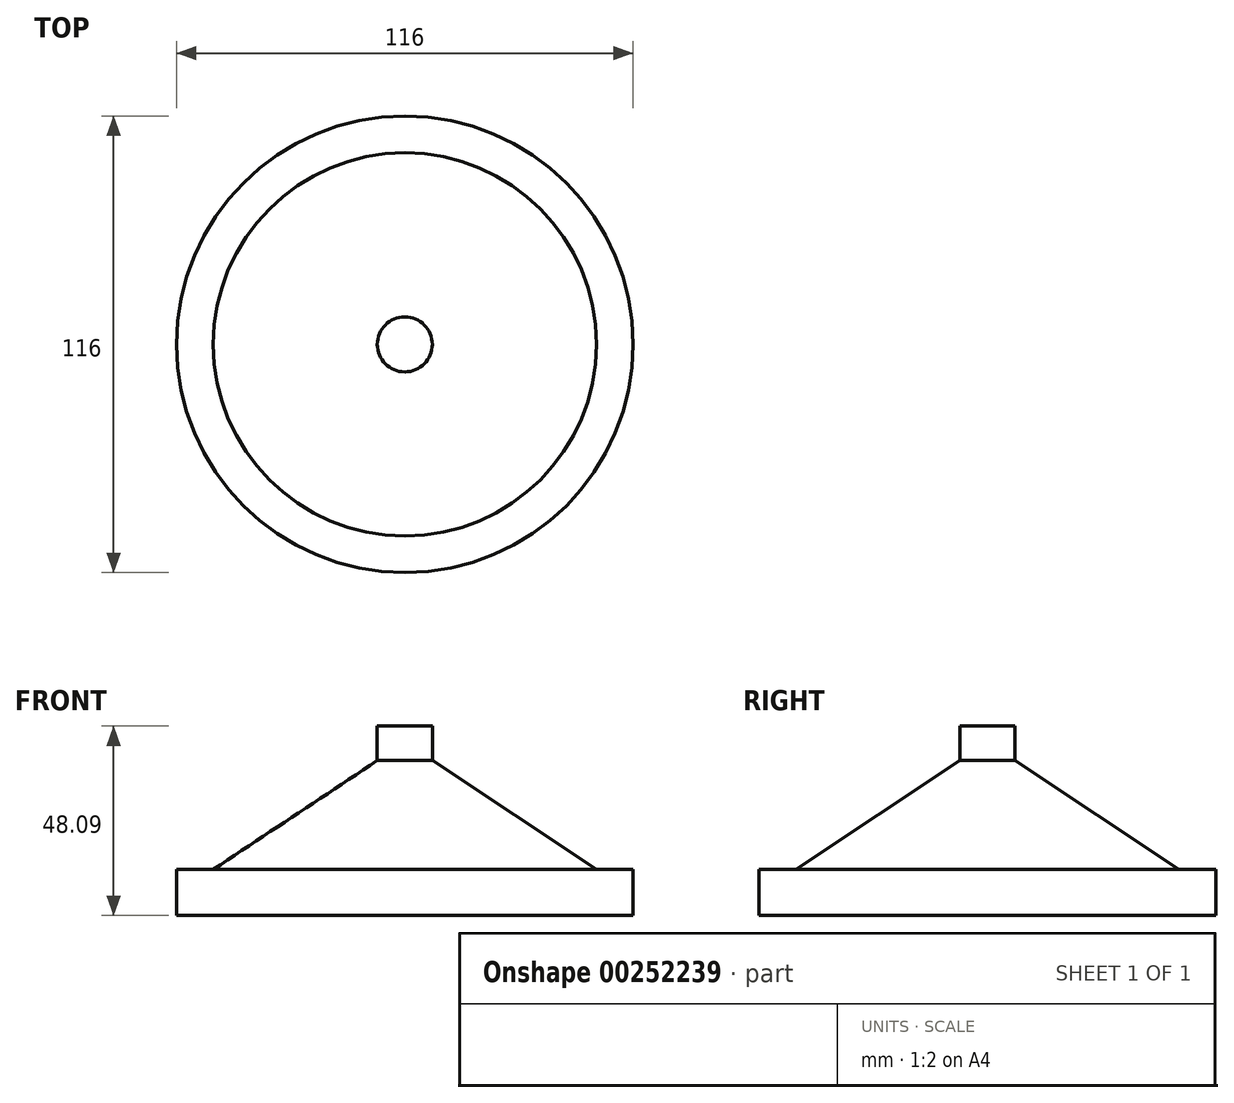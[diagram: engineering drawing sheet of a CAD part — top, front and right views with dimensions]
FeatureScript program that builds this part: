
annotation { "Feature Type Name" : "Feature", "Feature Type Description" : "" }
export const myFeature = defineFeature(function(context is Context, id is Id, definition is map)
    precondition{}
    {
        {
            var Q0;
            Q0=qCreatedBy(makeId("Front.planeOp"),FACE);
            var sketch = newSketch(context, id + "F0", { "sketchPlane" : qUnion([Q0])});
            skLineSegment(sketch, "E0", {"start": v(0, -8.9) * mm, "end": v(-7, -8.9) * mm});
            skLineSegment(sketch, "E1", {"start": v(-7, -10.35) * mm, "end": v(-7, -17.63) * mm});
            skLineSegment(sketch, "E2", {"start": v(-7, -17.63) * mm, "end": v(-48.68, -45.32) * mm});
            skLineSegment(sketch, "E3", {"start": v(-48.68, -45.32) * mm, "end": v(-58, -45.32) * mm});
            skLineSegment(sketch, "E4", {"start": v(-58, -45.32) * mm, "end": v(-58, -56.98) * mm});
            skLineSegment(sketch, "E5", {"start": v(-58.88, -56.98) * mm, "end": v(0, -56.98) * mm});
            skLineSegment(sketch, "E6", {"start": v(0, -56.98) * mm, "end": v(0, -8.9) * mm});
            skLineSegment(sketch, "E7", {"start": v(-7, -8.9) * mm, "end": v(-7, -10.35) * mm});
            skSolve(sketch);
        }
        {
            var Q0;
            Q0 = qSketchRegion(id + "F0", true);
            var Q1;
            Q1=sQuery(id+"F0.wireOp",EDGE,"E6");
            revolve(context, id + "F1", {"entities" : qUnion([Q0]), "axis" : qUnion([Q1]), "revolveType" : RevolveType.FULL});
        }
    });
